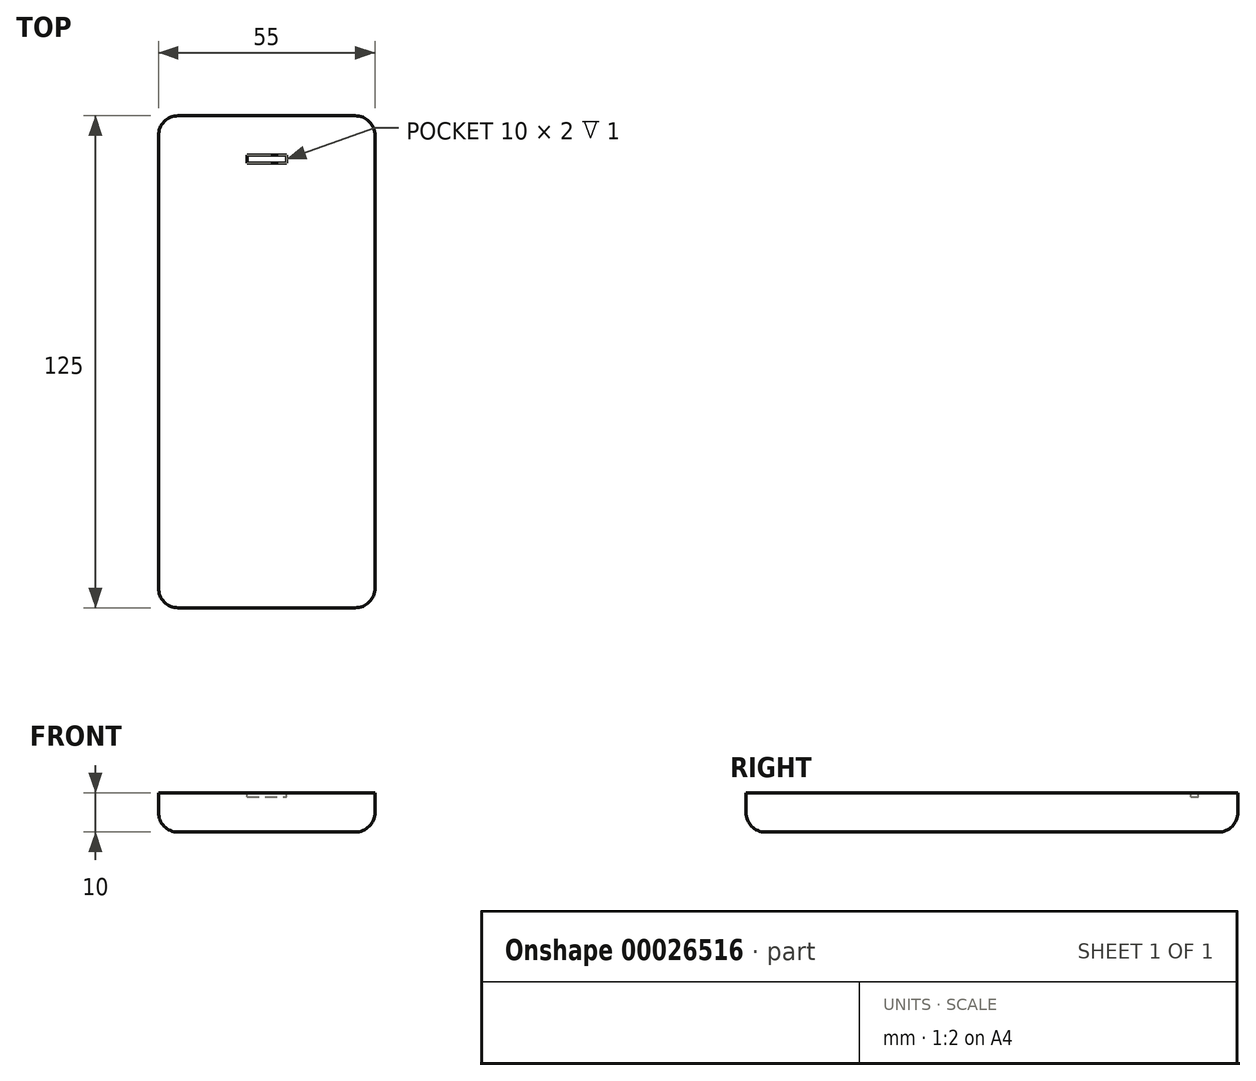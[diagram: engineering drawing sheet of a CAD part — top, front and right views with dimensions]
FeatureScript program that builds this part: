
annotation { "Feature Type Name" : "Feature", "Feature Type Description" : "" }
export const myFeature = defineFeature(function(context is Context, id is Id, definition is map)
    precondition{}
    {
        {
            var Q0;
            Q0=qCreatedBy(makeId("Top.planeOp"),FACE);
            var sketch = newSketch(context, id + "F0", { "sketchPlane" : qUnion([Q0])});
            skLineSegment(sketch, "E0.rect.bottom", {"start": v(-27.5, 62.5) * mm, "end": v(27.5, 62.5) * mm});
            skLineSegment(sketch, "E0.rect.top", {"start": v(-27.5, -62.5) * mm, "end": v(27.5, -62.5) * mm});
            skLineSegment(sketch, "E0.rect.left", {"start": v(-27.5, 62.5) * mm, "end": v(-27.5, -62.5) * mm});
            skLineSegment(sketch, "E0.rect.right", {"start": v(27.5, 62.5) * mm, "end": v(27.5, -62.5) * mm});
            skPoint(sketch, "E0.rect.middle", {"position": v(0, 0) * mm});
            skSolve(sketch);
        }
        {
            var Q0;
            Q0=makeQuery(id+"F0.imprint","IMPRINT",FACE,{"disambiguationData":[TD([[makeQuery(id+"F0.imprint","IMPRINT",EDGE,{"derivedFrom":sQuery(id+"F0.wireOp",EDGE,"E0.rect.bottom")}),-1.0]])]});
            extrude(context, id + "F1", {"entities" : qUnion([Q0]), "depth" : 10 * mm});
        }
        {
            var Q0;
            Q0=makeQuery(id+"F1.opExtrude","CAP_EDGE",EDGE,{"disambiguationData":[OSD([sQuery(id+"F0.wireOp",EDGE,"E0.rect.top")])],"isStart":true});
            var Q1;
            Q1=makeQuery(id+"F1.opExtrude","CAP_EDGE",EDGE,{"disambiguationData":[OSD([sQuery(id+"F0.wireOp",EDGE,"E0.rect.right")])],"isStart":true});
            var Q2;
            Q2=makeQuery(id+"F1.opExtrude","SWEPT_EDGE",EDGE,{"disambiguationData":[OSD([sQuery(id+"F0.wireOp",EDGE,"E0.rect.bottom"),sQuery(id+"F0.wireOp",EDGE,"E0.rect.right")])]});
            var Q3;
            Q3=makeQuery(id+"F1.opExtrude","SWEPT_EDGE",EDGE,{"disambiguationData":[OSD([sQuery(id+"F0.wireOp",EDGE,"E0.rect.top"),sQuery(id+"F0.wireOp",EDGE,"E0.rect.right")])]});
            var Q4;
            Q4=makeQuery(id+"F1.opExtrude","SWEPT_EDGE",EDGE,{"disambiguationData":[OSD([sQuery(id+"F0.wireOp",EDGE,"E0.rect.top"),sQuery(id+"F0.wireOp",EDGE,"E0.rect.left")])]});
            var Q5;
            Q5=makeQuery(id+"F1.opExtrude","CAP_EDGE",EDGE,{"disambiguationData":[OSD([sQuery(id+"F0.wireOp",EDGE,"E0.rect.left")])],"isStart":true});
            var Q6;
            Q6=makeQuery(id+"F1.opExtrude","CAP_EDGE",EDGE,{"disambiguationData":[OSD([sQuery(id+"F0.wireOp",EDGE,"E0.rect.bottom")])],"isStart":true});
            var Q7;
            Q7=makeQuery(id+"F1.opExtrude","SWEPT_EDGE",EDGE,{"disambiguationData":[OSD([sQuery(id+"F0.wireOp",EDGE,"E0.rect.bottom"),sQuery(id+"F0.wireOp",EDGE,"E0.rect.left")])]});
            fillet(context, id + "F2", {"entities" : qUnion([Q0, Q1, Q2, Q3, Q4, Q5, Q6, Q7]), "radius" : 5 * mm, "tangentPropagation" : true, "allowEdgeOverflow" : false});
        }
        {
            var Q0;
            Q0=makeQuery(id+"F1.opExtrude","CAP_FACE",FACE,{"disambiguationData":[OSD([sQuery(id+"F0.wireOp",EDGE,"E0.rect.bottom"),sQuery(id+"F0.wireOp",EDGE,"E0.rect.top"),sQuery(id+"F0.wireOp",EDGE,"E0.rect.left"),sQuery(id+"F0.wireOp",EDGE,"E0.rect.right")])],"isStart":false});
            var sketch = newSketch(context, id + "F3", { "sketchPlane" : qUnion([Q0])});
            skCircle(sketch, "E1", {"center": v(0, -52.5) * mm, "radius": 5 * mm});
            skSolve(sketch);
        }
        {
            var Q0;
            Q0=makeQuery(id+"F3.imprint","IMPRINT",FACE,{"disambiguationData":[TD([[makeQuery(id+"F3.imprint","IMPRINT",EDGE,{"derivedFrom":sQuery(id+"F3.wireOp",EDGE,"E1")}),-1.0]])]});
            var sketch = newSketch(context, id + "F4", { "sketchPlane" : qUnion([Q0])});
            skLineSegment(sketch, "E2.rect.bottom", {"start": v(-5, 50.5) * mm, "end": v(5, 50.5) * mm});
            skLineSegment(sketch, "E2.rect.top", {"start": v(-5, 52.5) * mm, "end": v(5, 52.5) * mm});
            skLineSegment(sketch, "E2.rect.left", {"start": v(-5, 50.5) * mm, "end": v(-5, 52.5) * mm});
            skLineSegment(sketch, "E2.rect.right", {"start": v(5, 50.5) * mm, "end": v(5, 52.5) * mm});
            skPoint(sketch, "E2.rect.middle", {"position": v(0, 51.5) * mm});
            skSolve(sketch);
        }
        {
            var Q0;
            Q0=makeQuery(id+"F4.imprint","IMPRINT",FACE,{"disambiguationData":[TD([[makeQuery(id+"F4.imprint","IMPRINT",EDGE,{"derivedFrom":sQuery(id+"F4.wireOp",EDGE,"E2.rect.bottom")}),1.0]])]});
            extrude(context, id + "F5", {"entities" : qUnion([Q0]), "operationType" : NewBodyOperationType.REMOVE, "oppositeDirection" : true, "depth" : 1 * mm});
        }
    });
